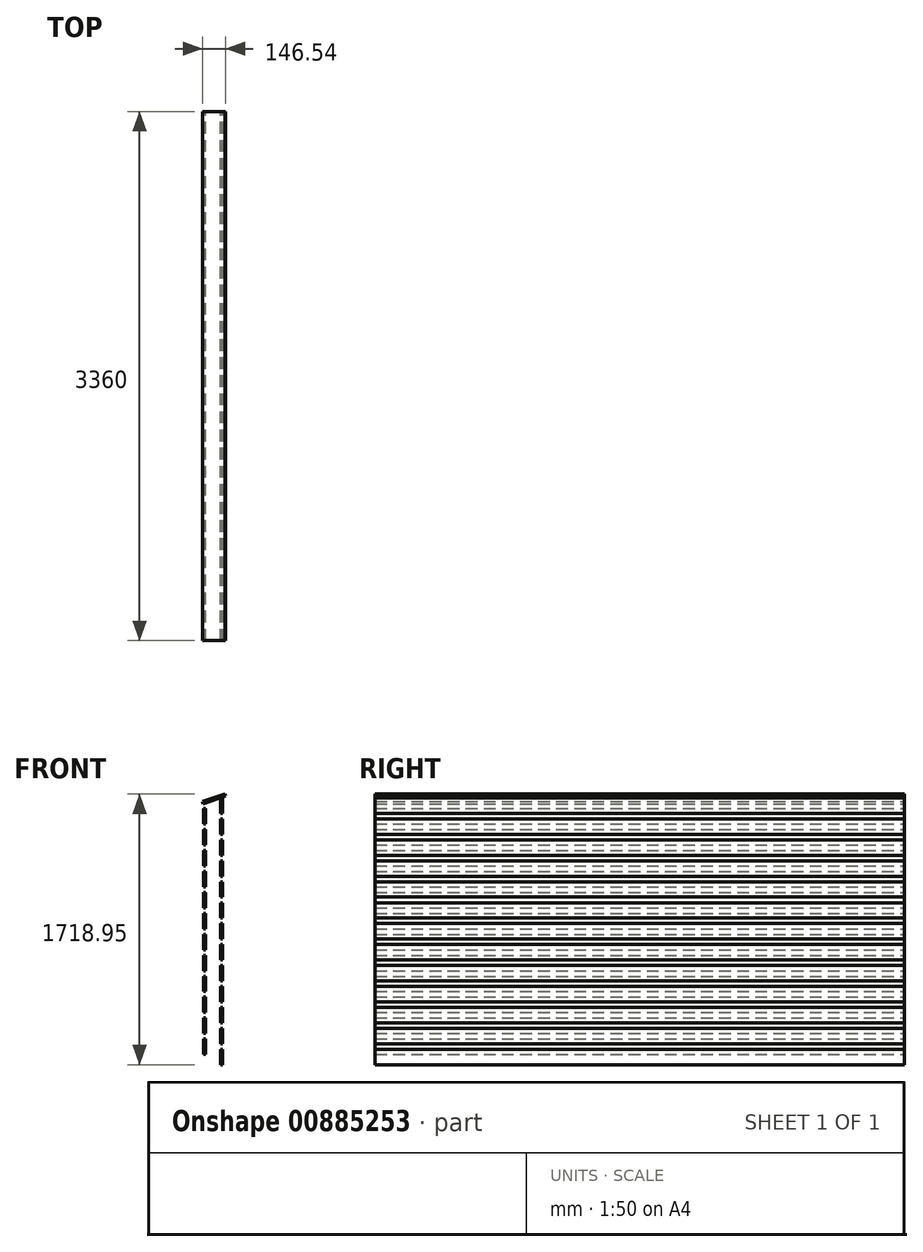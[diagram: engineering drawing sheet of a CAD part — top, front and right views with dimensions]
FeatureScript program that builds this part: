
annotation { "Feature Type Name" : "Feature", "Feature Type Description" : "" }
export const myFeature = defineFeature(function(context is Context, id is Id, definition is map)
    precondition{}
    {
        {
            var Q0;
            Q0=qCreatedBy(makeId("Front.planeOp"),FACE);
            var sketch = newSketch(context, id + "F0", { "sketchPlane" : qUnion([Q0])});
            skLineSegment(sketch, "E0.bottom", {"start": v(0, 98) * mm, "end": v(10, 98) * mm});
            skLineSegment(sketch, "E0.top", {"start": v(0, 0) * mm, "end": v(10, 0) * mm});
            skLineSegment(sketch, "E0.left", {"start": v(0, 98) * mm, "end": v(0, 0) * mm});
            skLineSegment(sketch, "E0.right", {"start": v(10, 98) * mm, "end": v(10, 0) * mm});
            skLineSegment(sketch, "E1.bottom", {"start": v(-108, 163) * mm, "end": v(-98, 163) * mm});
            skLineSegment(sketch, "E1.top", {"start": v(-108, 65) * mm, "end": v(-98, 65) * mm});
            skLineSegment(sketch, "E1.left", {"start": v(-108, 163) * mm, "end": v(-108, 65) * mm});
            skLineSegment(sketch, "E1.right", {"start": v(-98, 163) * mm, "end": v(-98, 65) * mm});
            skLineSegment(sketch, "E2.0.1.0", {"start": v(10, 231) * mm, "end": v(10, 133) * mm});
            skLineSegment(sketch, "E2.0.1.1", {"start": v(-108, 296) * mm, "end": v(-108, 198) * mm});
            skLineSegment(sketch, "E2.0.1.2", {"start": v(0, 231) * mm, "end": v(0, 133) * mm});
            skLineSegment(sketch, "E2.0.1.3", {"start": v(-98, 296) * mm, "end": v(-98, 198) * mm});
            skLineSegment(sketch, "E2.0.1.4", {"start": v(0, 231) * mm, "end": v(10, 231) * mm});
            skLineSegment(sketch, "E2.0.1.5", {"start": v(-108, 296) * mm, "end": v(-98, 296) * mm});
            skLineSegment(sketch, "E2.0.1.6", {"start": v(0, 133) * mm, "end": v(10, 133) * mm});
            skLineSegment(sketch, "E2.0.1.7", {"start": v(-108, 198) * mm, "end": v(-98, 198) * mm});
            skLineSegment(sketch, "E2.0.2.0", {"start": v(10, 364) * mm, "end": v(10, 266) * mm});
            skLineSegment(sketch, "E2.0.2.1", {"start": v(-108, 429) * mm, "end": v(-108, 331) * mm});
            skLineSegment(sketch, "E2.0.2.2", {"start": v(0, 364) * mm, "end": v(0, 266) * mm});
            skLineSegment(sketch, "E2.0.2.3", {"start": v(-98, 429) * mm, "end": v(-98, 331) * mm});
            skLineSegment(sketch, "E2.0.2.4", {"start": v(0, 364) * mm, "end": v(10, 364) * mm});
            skLineSegment(sketch, "E2.0.2.5", {"start": v(-108, 429) * mm, "end": v(-98, 429) * mm});
            skLineSegment(sketch, "E2.0.2.6", {"start": v(0, 266) * mm, "end": v(10, 266) * mm});
            skLineSegment(sketch, "E2.0.2.7", {"start": v(-108, 331) * mm, "end": v(-98, 331) * mm});
            skLineSegment(sketch, "E2.0.3.0", {"start": v(10, 497) * mm, "end": v(10, 399) * mm});
            skLineSegment(sketch, "E2.0.3.1", {"start": v(-108, 562) * mm, "end": v(-108, 464) * mm});
            skLineSegment(sketch, "E2.0.3.2", {"start": v(0, 497) * mm, "end": v(0, 399) * mm});
            skLineSegment(sketch, "E2.0.3.3", {"start": v(-98, 562) * mm, "end": v(-98, 464) * mm});
            skLineSegment(sketch, "E2.0.3.4", {"start": v(0, 497) * mm, "end": v(10, 497) * mm});
            skLineSegment(sketch, "E2.0.3.5", {"start": v(-108, 562) * mm, "end": v(-98, 562) * mm});
            skLineSegment(sketch, "E2.0.3.6", {"start": v(0, 399) * mm, "end": v(10, 399) * mm});
            skLineSegment(sketch, "E2.0.3.7", {"start": v(-108, 464) * mm, "end": v(-98, 464) * mm});
            skLineSegment(sketch, "E2.0.4.0", {"start": v(10, 630) * mm, "end": v(10, 532) * mm});
            skLineSegment(sketch, "E2.0.4.1", {"start": v(-108, 695) * mm, "end": v(-108, 597) * mm});
            skLineSegment(sketch, "E2.0.4.2", {"start": v(0, 630) * mm, "end": v(0, 532) * mm});
            skLineSegment(sketch, "E2.0.4.3", {"start": v(-98, 695) * mm, "end": v(-98, 597) * mm});
            skLineSegment(sketch, "E2.0.4.4", {"start": v(0, 630) * mm, "end": v(10, 630) * mm});
            skLineSegment(sketch, "E2.0.4.5", {"start": v(-108, 695) * mm, "end": v(-98, 695) * mm});
            skLineSegment(sketch, "E2.0.4.6", {"start": v(0, 532) * mm, "end": v(10, 532) * mm});
            skLineSegment(sketch, "E2.0.4.7", {"start": v(-108, 597) * mm, "end": v(-98, 597) * mm});
            skLineSegment(sketch, "E2.0.5.0", {"start": v(10, 763) * mm, "end": v(10, 665) * mm});
            skLineSegment(sketch, "E2.0.5.1", {"start": v(-108, 828) * mm, "end": v(-108, 730) * mm});
            skLineSegment(sketch, "E2.0.5.2", {"start": v(0, 763) * mm, "end": v(0, 665) * mm});
            skLineSegment(sketch, "E2.0.5.3", {"start": v(-98, 828) * mm, "end": v(-98, 730) * mm});
            skLineSegment(sketch, "E2.0.5.4", {"start": v(0, 763) * mm, "end": v(10, 763) * mm});
            skLineSegment(sketch, "E2.0.5.5", {"start": v(-108, 828) * mm, "end": v(-98, 828) * mm});
            skLineSegment(sketch, "E2.0.5.6", {"start": v(0, 665) * mm, "end": v(10, 665) * mm});
            skLineSegment(sketch, "E2.0.5.7", {"start": v(-108, 730) * mm, "end": v(-98, 730) * mm});
            skLineSegment(sketch, "E2.0.6.0", {"start": v(10, 896) * mm, "end": v(10, 798) * mm});
            skLineSegment(sketch, "E2.0.6.1", {"start": v(-108, 961) * mm, "end": v(-108, 863) * mm});
            skLineSegment(sketch, "E2.0.6.2", {"start": v(0, 896) * mm, "end": v(0, 798) * mm});
            skLineSegment(sketch, "E2.0.6.3", {"start": v(-98, 961) * mm, "end": v(-98, 863) * mm});
            skLineSegment(sketch, "E2.0.6.4", {"start": v(0, 896) * mm, "end": v(10, 896) * mm});
            skLineSegment(sketch, "E2.0.6.5", {"start": v(-108, 961) * mm, "end": v(-98, 961) * mm});
            skLineSegment(sketch, "E2.0.6.6", {"start": v(0, 798) * mm, "end": v(10, 798) * mm});
            skLineSegment(sketch, "E2.0.6.7", {"start": v(-108, 863) * mm, "end": v(-98, 863) * mm});
            skLineSegment(sketch, "E2.0.7.0", {"start": v(10, 1029) * mm, "end": v(10, 931) * mm});
            skLineSegment(sketch, "E2.0.7.1", {"start": v(-108, 1094) * mm, "end": v(-108, 996) * mm});
            skLineSegment(sketch, "E2.0.7.2", {"start": v(0, 1029) * mm, "end": v(0, 931) * mm});
            skLineSegment(sketch, "E2.0.7.3", {"start": v(-98, 1094) * mm, "end": v(-98, 996) * mm});
            skLineSegment(sketch, "E2.0.7.4", {"start": v(0, 1029) * mm, "end": v(10, 1029) * mm});
            skLineSegment(sketch, "E2.0.7.5", {"start": v(-108, 1094) * mm, "end": v(-98, 1094) * mm});
            skLineSegment(sketch, "E2.0.7.6", {"start": v(0, 931) * mm, "end": v(10, 931) * mm});
            skLineSegment(sketch, "E2.0.7.7", {"start": v(-108, 996) * mm, "end": v(-98, 996) * mm});
            skLineSegment(sketch, "E2.0.8.0", {"start": v(10, 1162) * mm, "end": v(10, 1064) * mm});
            skLineSegment(sketch, "E2.0.8.1", {"start": v(-108, 1227) * mm, "end": v(-108, 1129) * mm});
            skLineSegment(sketch, "E2.0.8.2", {"start": v(0, 1162) * mm, "end": v(0, 1064) * mm});
            skLineSegment(sketch, "E2.0.8.3", {"start": v(-98, 1227) * mm, "end": v(-98, 1129) * mm});
            skLineSegment(sketch, "E2.0.8.4", {"start": v(0, 1162) * mm, "end": v(10, 1162) * mm});
            skLineSegment(sketch, "E2.0.8.5", {"start": v(-108, 1227) * mm, "end": v(-98, 1227) * mm});
            skLineSegment(sketch, "E2.0.8.6", {"start": v(0, 1064) * mm, "end": v(10, 1064) * mm});
            skLineSegment(sketch, "E2.0.8.7", {"start": v(-108, 1129) * mm, "end": v(-98, 1129) * mm});
            skLineSegment(sketch, "E2.0.9.0", {"start": v(10, 1295) * mm, "end": v(10, 1197) * mm});
            skLineSegment(sketch, "E2.0.9.1", {"start": v(-108, 1360) * mm, "end": v(-108, 1262) * mm});
            skLineSegment(sketch, "E2.0.9.2", {"start": v(0, 1295) * mm, "end": v(0, 1197) * mm});
            skLineSegment(sketch, "E2.0.9.3", {"start": v(-98, 1360) * mm, "end": v(-98, 1262) * mm});
            skLineSegment(sketch, "E2.0.9.4", {"start": v(0, 1295) * mm, "end": v(10, 1295) * mm});
            skLineSegment(sketch, "E2.0.9.5", {"start": v(-108, 1360) * mm, "end": v(-98, 1360) * mm});
            skLineSegment(sketch, "E2.0.9.6", {"start": v(0, 1197) * mm, "end": v(10, 1197) * mm});
            skLineSegment(sketch, "E2.0.9.7", {"start": v(-108, 1262) * mm, "end": v(-98, 1262) * mm});
            skLineSegment(sketch, "E2.0.10.0", {"start": v(10, 1428) * mm, "end": v(10, 1330) * mm});
            skLineSegment(sketch, "E2.0.10.1", {"start": v(-108, 1493) * mm, "end": v(-108, 1395) * mm});
            skLineSegment(sketch, "E2.0.10.2", {"start": v(0, 1428) * mm, "end": v(0, 1330) * mm});
            skLineSegment(sketch, "E2.0.10.3", {"start": v(-98, 1493) * mm, "end": v(-98, 1395) * mm});
            skLineSegment(sketch, "E2.0.10.4", {"start": v(0, 1428) * mm, "end": v(10, 1428) * mm});
            skLineSegment(sketch, "E2.0.10.5", {"start": v(-108, 1493) * mm, "end": v(-98, 1493) * mm});
            skLineSegment(sketch, "E2.0.10.6", {"start": v(0, 1330) * mm, "end": v(10, 1330) * mm});
            skLineSegment(sketch, "E2.0.10.7", {"start": v(-108, 1395) * mm, "end": v(-98, 1395) * mm});
            skLineSegment(sketch, "E2.0.11.0", {"start": v(10, 1561) * mm, "end": v(10, 1463) * mm});
            skLineSegment(sketch, "E2.0.11.1", {"start": v(-108, 1626) * mm, "end": v(-108, 1528) * mm});
            skLineSegment(sketch, "E2.0.11.2", {"start": v(0, 1561) * mm, "end": v(0, 1463) * mm});
            skLineSegment(sketch, "E2.0.11.3", {"start": v(-98, 1626) * mm, "end": v(-98, 1528) * mm});
            skLineSegment(sketch, "E2.0.11.4", {"start": v(0, 1561) * mm, "end": v(10, 1561) * mm});
            skLineSegment(sketch, "E2.0.11.5", {"start": v(-108, 1626) * mm, "end": v(-98, 1626) * mm});
            skLineSegment(sketch, "E2.0.11.6", {"start": v(0, 1463) * mm, "end": v(10, 1463) * mm});
            skLineSegment(sketch, "E2.0.11.7", {"start": v(-108, 1528) * mm, "end": v(-98, 1528) * mm});
            skLineSegment(sketch, "E2.0.12.0", {"start": v(10, 1694) * mm, "end": v(10, 1596) * mm});
            skLineSegment(sketch, "E2.0.12.2", {"start": v(0, 1694) * mm, "end": v(0, 1596) * mm});
            skLineSegment(sketch, "E2.0.12.4", {"start": v(0, 1694) * mm, "end": v(10, 1694) * mm});
            skLineSegment(sketch, "E2.0.12.6", {"start": v(0, 1596) * mm, "end": v(10, 1596) * mm});
            skLineSegment(sketch, "E2.direction1", {"start": v(-108, 65) * mm, "end": v(-83, 65) * mm, "construction": true});
            skLineSegment(sketch, "E2.direction2", {"start": v(-108, 65) * mm, "end": v(-108, 198) * mm, "construction": true});
            skLineSegment(sketch, "E3", {"start": v(30.34, 1705.66) * mm, "end": v(-111.7, 1657.42) * mm});
            skLineSegment(sketch, "E4", {"start": v(-111.7, 1657.42) * mm, "end": v(-116.2, 1670.7) * mm});
            skLineSegment(sketch, "E5", {"start": v(-116.2, 1670.7) * mm, "end": v(25.83, 1718.95) * mm});
            skLineSegment(sketch, "E6", {"start": v(25.83, 1718.95) * mm, "end": v(30.34, 1705.66) * mm});
            skSolve(sketch);
        }
        {
            var Q0;
            Q0=makeQuery(id+"F0.imprint","IMPRINT",FACE,{"disambiguationData":[TD([[makeQuery(id+"F0.imprint","IMPRINT",EDGE,{"derivedFrom":sQuery(id+"F0.wireOp",EDGE,"E3")}),-1.0]])]});
            var Q1;
            Q1=makeQuery(id+"F0.imprint","IMPRINT",FACE,{"disambiguationData":[TD([[makeQuery(id+"F0.imprint","IMPRINT",EDGE,{"derivedFrom":sQuery(id+"F0.wireOp",EDGE,"E2.0.9.1")}),1.0]])]});
            var Q2;
            Q2=makeQuery(id+"F0.imprint","IMPRINT",FACE,{"disambiguationData":[TD([[makeQuery(id+"F0.imprint","IMPRINT",EDGE,{"derivedFrom":sQuery(id+"F0.wireOp",EDGE,"E2.0.2.1")}),1.0]])]});
            var Q3;
            Q3=makeQuery(id+"F0.imprint","IMPRINT",FACE,{"disambiguationData":[TD([[makeQuery(id+"F0.imprint","IMPRINT",EDGE,{"derivedFrom":sQuery(id+"F0.wireOp",EDGE,"E2.0.4.0")}),-1.0]])]});
            var Q4;
            Q4=makeQuery(id+"F0.imprint","IMPRINT",FACE,{"disambiguationData":[TD([[makeQuery(id+"F0.imprint","IMPRINT",EDGE,{"derivedFrom":sQuery(id+"F0.wireOp",EDGE,"E2.0.6.1")}),1.0]])]});
            var Q5;
            Q5=makeQuery(id+"F0.imprint","IMPRINT",FACE,{"disambiguationData":[TD([[makeQuery(id+"F0.imprint","IMPRINT",EDGE,{"derivedFrom":sQuery(id+"F0.wireOp",EDGE,"E2.0.5.0")}),-1.0]])]});
            var Q6;
            Q6=makeQuery(id+"F0.imprint","IMPRINT",FACE,{"disambiguationData":[TD([[makeQuery(id+"F0.imprint","IMPRINT",EDGE,{"derivedFrom":sQuery(id+"F0.wireOp",EDGE,"E2.0.5.1")}),1.0]])]});
            var Q7;
            Q7=makeQuery(id+"F0.imprint","IMPRINT",FACE,{"disambiguationData":[TD([[makeQuery(id+"F0.imprint","IMPRINT",EDGE,{"derivedFrom":sQuery(id+"F0.wireOp",EDGE,"E2.0.2.0")}),-1.0]])]});
            var Q8;
            Q8=makeQuery(id+"F0.imprint","IMPRINT",FACE,{"disambiguationData":[TD([[makeQuery(id+"F0.imprint","IMPRINT",EDGE,{"derivedFrom":sQuery(id+"F0.wireOp",EDGE,"E2.0.8.0")}),-1.0]])]});
            var Q9;
            Q9=makeQuery(id+"F0.imprint","IMPRINT",FACE,{"disambiguationData":[TD([[makeQuery(id+"F0.imprint","IMPRINT",EDGE,{"derivedFrom":sQuery(id+"F0.wireOp",EDGE,"E2.0.11.0")}),-1.0]])]});
            var Q10;
            Q10=makeQuery(id+"F0.imprint","IMPRINT",FACE,{"disambiguationData":[TD([[makeQuery(id+"F0.imprint","IMPRINT",EDGE,{"derivedFrom":sQuery(id+"F0.wireOp",EDGE,"E2.0.9.0")}),-1.0]])]});
            var Q11;
            Q11=makeQuery(id+"F0.imprint","IMPRINT",FACE,{"disambiguationData":[TD([[makeQuery(id+"F0.imprint","IMPRINT",EDGE,{"derivedFrom":sQuery(id+"F0.wireOp",EDGE,"E1.bottom")}),-1.0]])]});
            var Q12;
            Q12=makeQuery(id+"F0.imprint","IMPRINT",FACE,{"disambiguationData":[TD([[makeQuery(id+"F0.imprint","IMPRINT",EDGE,{"derivedFrom":sQuery(id+"F0.wireOp",EDGE,"E2.0.6.0")}),-1.0]])]});
            var Q13;
            Q13=makeQuery(id+"F0.imprint","IMPRINT",FACE,{"disambiguationData":[TD([[makeQuery(id+"F0.imprint","IMPRINT",EDGE,{"derivedFrom":sQuery(id+"F0.wireOp",EDGE,"E2.0.7.0")}),-1.0]])]});
            var Q14;
            Q14=makeQuery(id+"F0.imprint","IMPRINT",FACE,{"disambiguationData":[TD([[makeQuery(id+"F0.imprint","IMPRINT",EDGE,{"derivedFrom":sQuery(id+"F0.wireOp",EDGE,"E2.0.10.1")}),1.0]])]});
            var Q15;
            Q15=makeQuery(id+"F0.imprint","IMPRINT",FACE,{"disambiguationData":[TD([[makeQuery(id+"F0.imprint","IMPRINT",EDGE,{"derivedFrom":sQuery(id+"F0.wireOp",EDGE,"E2.0.8.1")}),1.0]])]});
            var Q16;
            Q16=makeQuery(id+"F0.imprint","IMPRINT",FACE,{"disambiguationData":[TD([[makeQuery(id+"F0.imprint","IMPRINT",EDGE,{"derivedFrom":sQuery(id+"F0.wireOp",EDGE,"E2.0.12.0")}),-1.0]])]});
            var Q17;
            Q17=makeQuery(id+"F0.imprint","IMPRINT",FACE,{"disambiguationData":[TD([[makeQuery(id+"F0.imprint","IMPRINT",EDGE,{"derivedFrom":sQuery(id+"F0.wireOp",EDGE,"E2.0.1.1")}),1.0]])]});
            var Q18;
            Q18=makeQuery(id+"F0.imprint","IMPRINT",FACE,{"disambiguationData":[TD([[makeQuery(id+"F0.imprint","IMPRINT",EDGE,{"derivedFrom":sQuery(id+"F0.wireOp",EDGE,"E0.bottom")}),-1.0]])]});
            var Q19;
            Q19=makeQuery(id+"F0.imprint","IMPRINT",FACE,{"disambiguationData":[TD([[makeQuery(id+"F0.imprint","IMPRINT",EDGE,{"derivedFrom":sQuery(id+"F0.wireOp",EDGE,"E2.0.4.1")}),1.0]])]});
            var Q20;
            Q20=makeQuery(id+"F0.imprint","IMPRINT",FACE,{"disambiguationData":[TD([[makeQuery(id+"F0.imprint","IMPRINT",EDGE,{"derivedFrom":sQuery(id+"F0.wireOp",EDGE,"E2.0.10.0")}),-1.0]])]});
            var Q21;
            Q21=makeQuery(id+"F0.imprint","IMPRINT",FACE,{"disambiguationData":[TD([[makeQuery(id+"F0.imprint","IMPRINT",EDGE,{"derivedFrom":sQuery(id+"F0.wireOp",EDGE,"E2.0.11.1")}),1.0]])]});
            var Q22;
            Q22=makeQuery(id+"F0.imprint","IMPRINT",FACE,{"disambiguationData":[TD([[makeQuery(id+"F0.imprint","IMPRINT",EDGE,{"derivedFrom":sQuery(id+"F0.wireOp",EDGE,"E2.0.3.1")}),1.0]])]});
            var Q23;
            Q23=makeQuery(id+"F0.imprint","IMPRINT",FACE,{"disambiguationData":[TD([[makeQuery(id+"F0.imprint","IMPRINT",EDGE,{"derivedFrom":sQuery(id+"F0.wireOp",EDGE,"E2.0.3.0")}),-1.0]])]});
            var Q24;
            Q24=makeQuery(id+"F0.imprint","IMPRINT",FACE,{"disambiguationData":[TD([[makeQuery(id+"F0.imprint","IMPRINT",EDGE,{"derivedFrom":sQuery(id+"F0.wireOp",EDGE,"E2.0.1.0")}),-1.0]])]});
            var Q25;
            Q25=makeQuery(id+"F0.imprint","IMPRINT",FACE,{"disambiguationData":[TD([[makeQuery(id+"F0.imprint","IMPRINT",EDGE,{"derivedFrom":sQuery(id+"F0.wireOp",EDGE,"E2.0.7.1")}),1.0]])]});
            extrude(context, id + "F1", {"entities" : qUnion([Q0, Q1, Q2, Q3, Q4, Q5, Q6, Q7, Q8, Q9, Q10, Q11, Q12, Q13, Q14, Q15, Q16, Q17, Q18, Q19, Q20, Q21, Q22, Q23, Q24, Q25]), "depth" : 3360 * mm, "offsetDistance" : 25 * mm});
        }
    });
